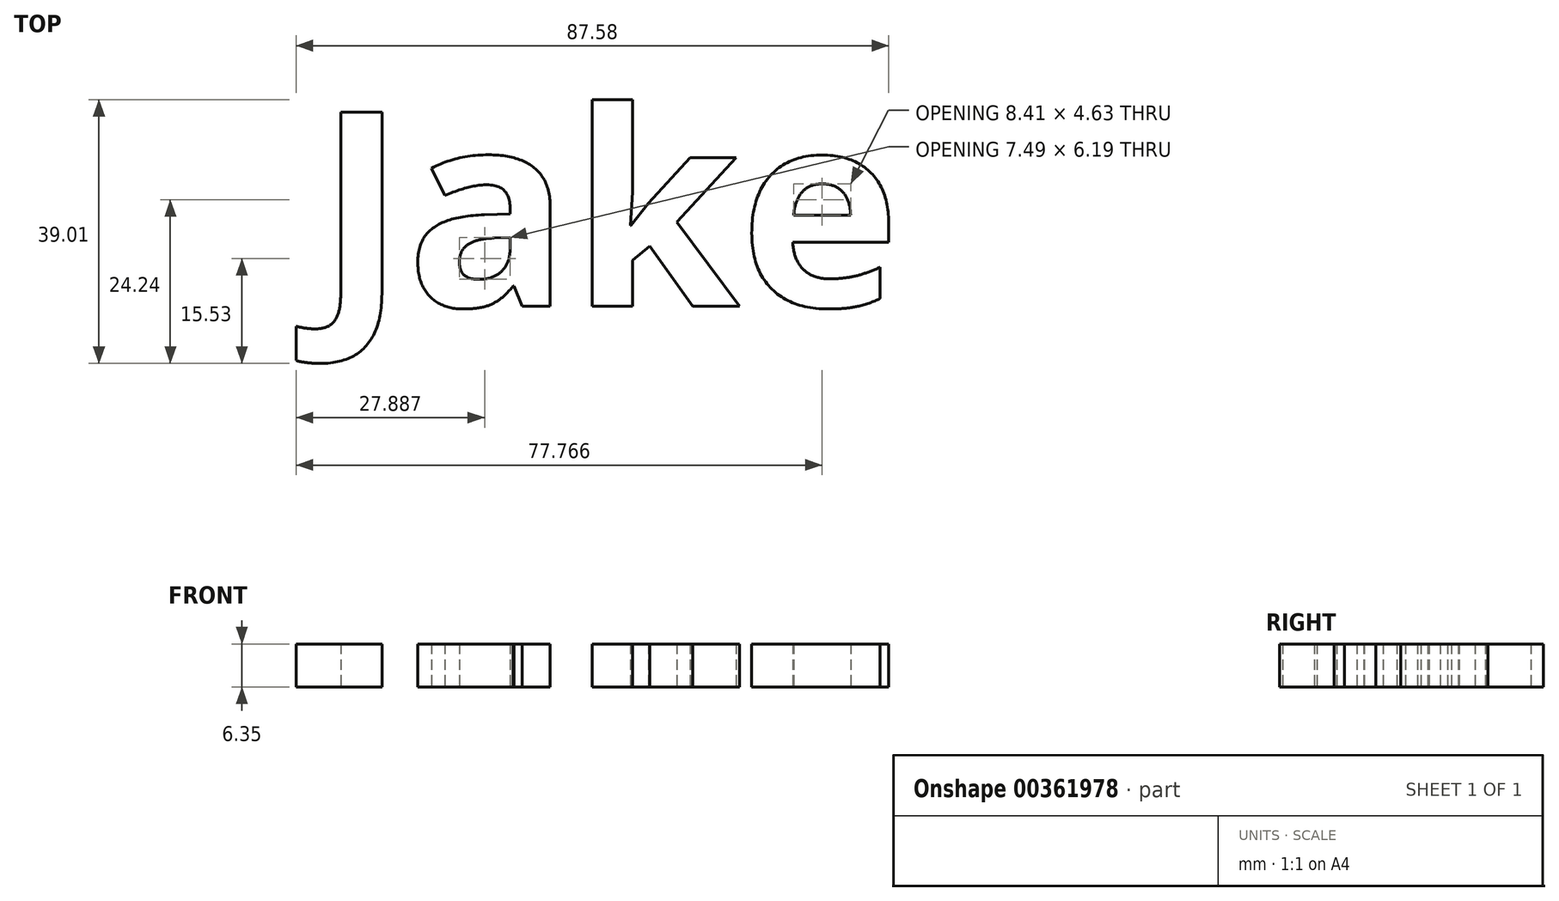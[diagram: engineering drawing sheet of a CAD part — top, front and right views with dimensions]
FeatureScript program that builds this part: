
annotation { "Feature Type Name" : "Feature", "Feature Type Description" : "" }
export const myFeature = defineFeature(function(context is Context, id is Id, definition is map)
    precondition{}
    {
        {
            var Q0;
            Q0=qCreatedBy(makeId("Top.planeOp"),FACE);
            var sketch = newSketch(context, id + "F0", { "sketchPlane" : qUnion([Q0])});
            skText(sketch, "E0", { "text": "Jake", "fontName": "OpenSans-Bold.ttf"});
            const initialGuessF0  = {"E0": [-0.03018, -0.01905, 1, 0, 0.02896]};
            skSetInitialGuess(sketch, initialGuessF0);
            skSolve(sketch);
        }
        {
            var Q0;
            Q0 = qSketchRegion(id + "F0", true);
            extrude(context, id + "F1", {"entities" : qUnion([Q0]), "depth" : 6.35 * mm});
        }
    });
